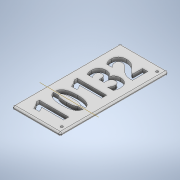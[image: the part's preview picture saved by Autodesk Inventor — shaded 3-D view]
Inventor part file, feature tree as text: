
AUTODESK INVENTOR PART (.ipt)
format: ipt  version: 2020 (Build 240168000, 168)  size: 277,504 bytes
history: native  units: in
note: dims shown in document units (in); Inventor stores cm internally (conversion verified against a paired STEP export)
features: extrude x3, sketch x3, emboss x1, other x1, fillet x1, projected_geometry x1
ambient origin geometry x8: Origin, YZ Plane, XZ Plane, XY Plane, X Axis, Y Axis, Z Axis, Center Point
bodies: Solid1 (feature_tree)
feature tree (10):
  extrude  "Extrusion1"  Depth=9.0in
  emboss  "Emboss1"
  other  "Work Axis1"
  extrude  "Extrusion2"  Depth=0.3in TaperAngle=0.0deg
  fillet  "Fillet1"  Radius=0.1in
  extrude  "Extrusion4"  Depth=0.3in TaperAngle=0.0deg
  sketch  "Sketch1"  dims[d0=4.0in d1=9.0in]
  sketch  "Sketch2"  dims[d2=0.3in d3=0.0in d4=0.3in d5=0.0in d6=0.1in]
  projected_geometry  "Projected Loop1"
  sketch  "Sketch9"  dims[d7=0.2in d8=0.3in d9=0.0in d16=0.125in d17=0.4in d18=0.4in d19=0.4in d20=0.4in d21=0.2in d22=0.2in d23=0.3in d24=0.0in]
